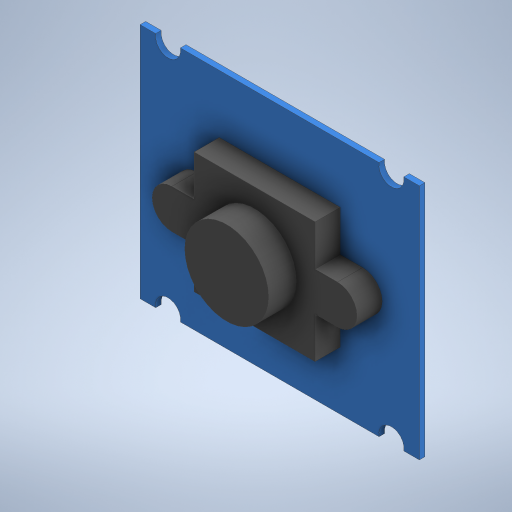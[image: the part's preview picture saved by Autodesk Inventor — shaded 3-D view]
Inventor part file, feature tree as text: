
AUTODESK INVENTOR PART (.ipt)
format: ipt  version: 2023 (Build 270158000, 158)  size: 300,544 bytes
history: native  units: mm
features: extrude x4, sketch x4, other x1
ambient origin geometry x8: Origin, YZ Plane, XZ Plane, XY Plane, X Axis, Y Axis, Z Axis, Center Point
bodies: Body1 (feature_tree)
feature tree (9):
  other  "솔리드1"
  extrude  "돌출1"  Depth=30.0mm
  extrude  "돌출2"  Depth=25.5mm
  extrude  "돌출3"  Depth=0.6mm TaperAngle=0.0deg
  extrude  "돌출4"  Depth=24.0mm
  sketch  "스케치1"
  sketch  "스케치2"
  sketch  "스케치3"
  sketch  "스케치4"
